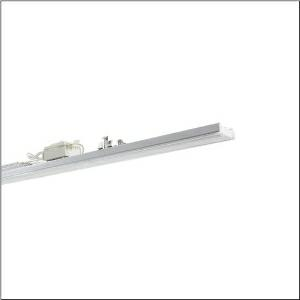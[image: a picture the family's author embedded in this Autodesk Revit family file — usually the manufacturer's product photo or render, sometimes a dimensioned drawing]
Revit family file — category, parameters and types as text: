
# Revit family: licross_11_recessed_mo_51te14dn49xg
name_source: partatom
category: Lighting Fixtures
units: mm (PartAtom-declared; Revit-internal decimal feet)

## family parameters
Cut with Voids When Loaded = No
Host = Face
Light Source = No
Part Type = Normal
Room Calculation Point = No
Round Connector Dimension = Use Diameter
Shared = No

## types (1)
- --- (1 x LED, 9430 lm, 56.7 W, 4000K)
    Apparent Load = 57 VA
    CIE Flux Codes = 56 84 97 100 100
    Color Rendering = 80
    Color Temperature = 4000K
    Default Elevation = 1800 mm
    Description = Licross 11 Recessed MO, luminaire insert, of sheet steel, galvanised, coil coated, white, length: 1.500mm, width: 66mm, height: 67mm, LED rated luminous flux: 9.430lm, light colour: 840, SDCM (Standard Deviation of Colour Matching)MacAdam ≤ 2 SDCM (initial), control gear: DALI 2, with plug, 5-pole, with phase selection, mains connection: 220..240V, AC, 50/60Hz, rated input power: 57W, internal wiring halogen-free, primary light control with lens, of plastic, primary optical cover: cover, of PMMA, light emission: direct distribution, primary light characteristic: asymmetric, protection rating (complete): IP54, insulation class (complete): insulation class I (protective earthing), certification: CE, ENEC, VDE, UKCA, protection symbol: D if used in an environment with non-conductive dust loads with corresponding accessories, impact resistance: IK06, permissible ambient temperature for indoor applications: -25..+35°C, corresponds to IFS (International Featured Standards) requirements for safety and quality in the food industry, reducing of maximum allowable ambient temperature of 5°C with ceiling mounting, LABS conformity tested according to VDMA 24364:2018-05, The light source and the operating device comply with the requirements of the Ecodesign Regulation (EU) 2019/2020 and are replaceable in accordance with this regulation, packaging unit: 1 piece
    Height = 58 mm
    Lamp = 1 x LED
    Lamp Light Flux = 9430 lm
    Lamp Power = 56.7 W
    Lamp count = 1
    Length = 1500 mm
    Luminous efficacy = 166 lm/W
    Manufacturer = Siteco
    ModVariant = No
    Model = 51TE14DN49XG
    Mounting Place = Ceiling
    Mounting Type = Pendant
    Number of Poles = 1
    OnlyDefault = Yes
    Power Factor = 1
    Product Name = Licross 11 Recessed MO
    Product group = luminaire insert | ceiling pendant
    ProductGroupID = 901
    Protection Class = Protection class I
    Protection Degree = IP 54
    RLX_Detail_Level = 1
    RLX_Emergency_Light_Flux = 0 lm
    RLX_Emergency_Type = 0
    RLX_Emergency_Type_DB = No
    RlxData = <blob elided: 25193 chars, md5=24b571c8>
    Socket = socket
    Standby Power = 0 W
    System Light Flux = 9430 lm
    System Power = 57 W
    Type Comments = factory setting: luminous flux: 100 % | dim-lin: 254 | 378 mA
    Type Image = l_1296930.jpg
    URL = http://relux.com
    VarID = @adj_101605
    Voltage = 0 V
    Weight = 0.00 kg
    Width = 66 mm

## geometry (parser evidence)
native form markers: Blend x4, Sweep x10
no freeform markers — native parametric forms only
